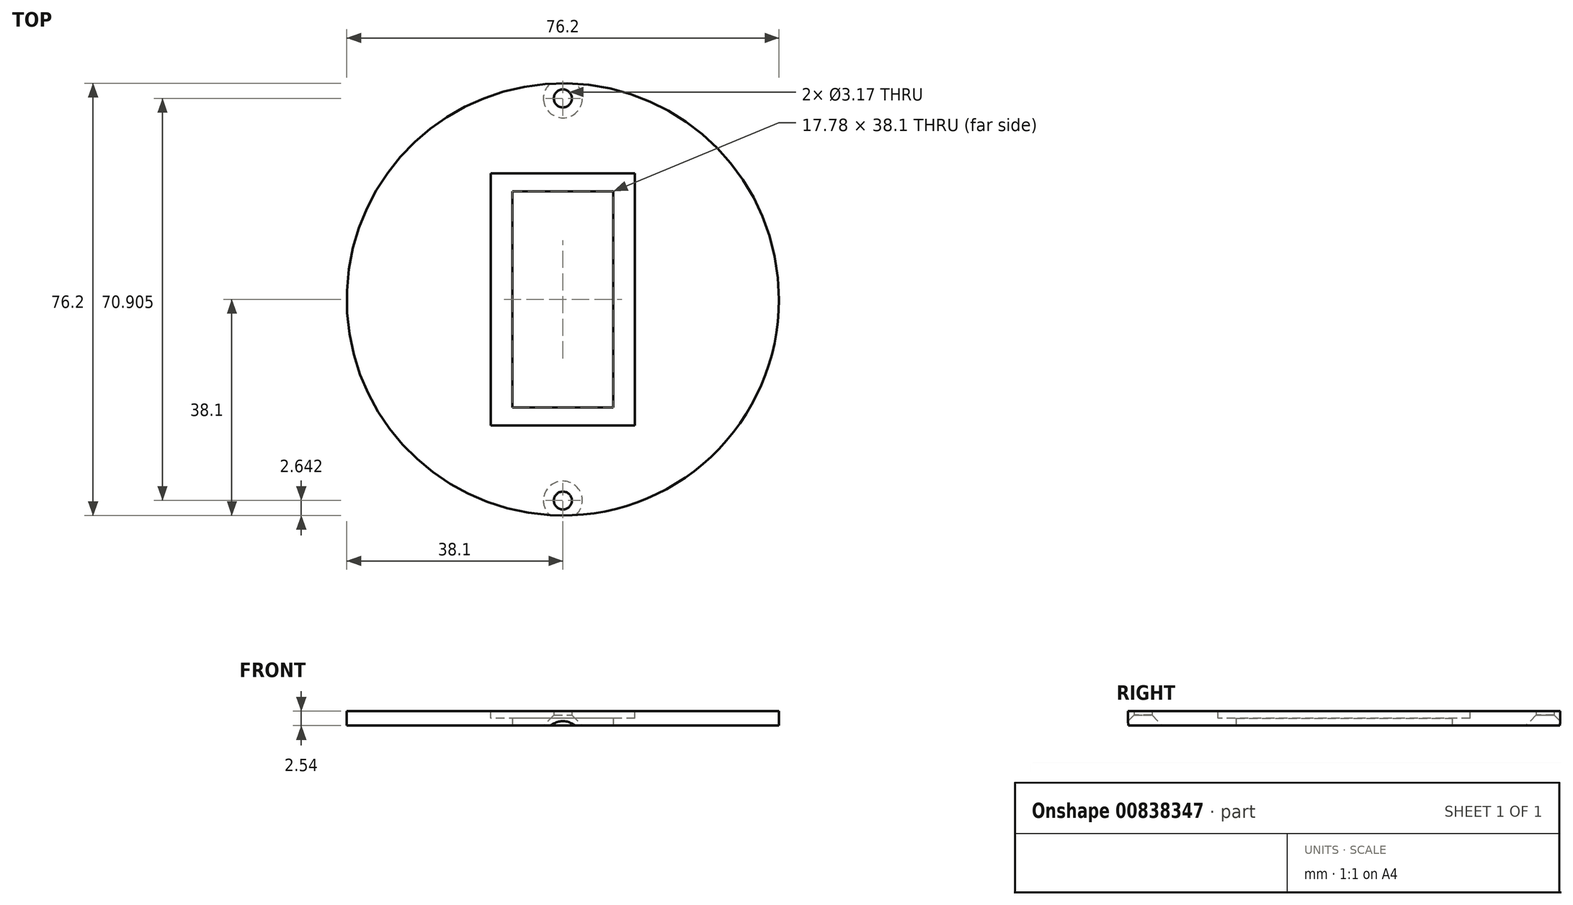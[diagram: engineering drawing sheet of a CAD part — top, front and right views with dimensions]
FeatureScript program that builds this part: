
annotation { "Feature Type Name" : "Feature", "Feature Type Description" : "" }
export const myFeature = defineFeature(function(context is Context, id is Id, definition is map)
    precondition{}
    {
        {
            var Q0;
            Q0=qCreatedBy(makeId("Top.planeOp"),FACE);
            var sketch = newSketch(context, id + "F0", { "sketchPlane" : qUnion([Q0])});
            skCircle(sketch, "E0", {"center": v(0, 0) * mm, "radius": 38.1 * mm});
            skLineSegment(sketch, "E1.bottom", {"start": v(8.9, -19.05) * mm, "end": v(-8.89, -19.05) * mm});
            skLineSegment(sketch, "E1.top", {"start": v(8.9, 19.05) * mm, "end": v(-8.89, 19.05) * mm});
            skLineSegment(sketch, "E1.left", {"start": v(8.9, -19.05) * mm, "end": v(8.9, 19.05) * mm});
            skLineSegment(sketch, "E1.right", {"start": v(-8.89, -19.05) * mm, "end": v(-8.89, 19.05) * mm});
            skSolve(sketch);
        }
        {
            var Q0;
            Q0=qCreatedBy(makeId("Top.planeOp"),FACE);
            var sketch = newSketch(context, id + "F1", { "sketchPlane" : qUnion([Q0])});
            skPoint(sketch, "E2", {"position": v(0, 35.45) * mm});
            skPoint(sketch, "E3", {"position": v(0, -35.46) * mm});
            skSolve(sketch);
        }
        {
            var Q0;
            Q0=makeQuery(id+"F0.imprint","IMPRINT",FACE,{"disambiguationData":[TD([[makeQuery(id+"F0.imprint","IMPRINT",EDGE,{"derivedFrom":sQuery(id+"F0.wireOp",EDGE,"E0")}),1.0]])]});
            extrude(context, id + "F2", {"entities" : qUnion([Q0]), "depth" : 2.54 * mm, "offsetDistance" : 25.4 * mm});
        }
        {
            var Q0;
            Q0=sQuery(id+"F1.wireOp",VERTEX,"E3");
            var Q1;
            Q1=sQuery(id+"F1.wireOp",VERTEX,"E2");
            var Q2;
            Q2=makeQuery(id+"F2.opExtrude","SWEPT_BODY",BODY,{"disambiguationData":[OSD([sQuery(id+"F0.wireOp",EDGE,"E0"),sQuery(id+"F0.wireOp",EDGE,"E1.bottom"),sQuery(id+"F0.wireOp",EDGE,"E1.top"),sQuery(id+"F0.wireOp",EDGE,"E1.left"),sQuery(id+"F0.wireOp",EDGE,"E1.right")])]});
            hole(context, id + "F3", {"style" : HoleStyle.C_SINK, "endStyle" : HoleEndStyle.THROUGH, "oppositeDirection" : true, "holeDiameter" : 3.17 * mm, "cSinkDiameter" : 6.86 * mm, "cSinkAngle" : 90 * degree, "majorDiameter" : 6.35 * mm, "isTappedThrough" : true, "tappedDepth" : 12.7 * mm, "tapClearance" : 3, "locations" : qUnion([Q0, Q1]), "scope" : qUnion([Q2])});
        }
        {
            var Q0;
            Q0=makeQuery(id+"F2.opExtrude","CAP_FACE",FACE,{"disambiguationData":[OSD([sQuery(id+"F0.wireOp",EDGE,"E0"),sQuery(id+"F0.wireOp",EDGE,"E1.bottom"),sQuery(id+"F0.wireOp",EDGE,"E1.top"),sQuery(id+"F0.wireOp",EDGE,"E1.left"),sQuery(id+"F0.wireOp",EDGE,"E1.right")])],"isStart":false});
            var sketch = newSketch(context, id + "F4", { "sketchPlane" : qUnion([Q0])});
            skLineSegment(sketch, "E4.bottom", {"start": v(12.7, 22.23) * mm, "end": v(-12.7, 22.23) * mm});
            skLineSegment(sketch, "E4.top", {"start": v(12.7, -22.23) * mm, "end": v(-12.7, -22.23) * mm});
            skLineSegment(sketch, "E4.left", {"start": v(12.7, 22.23) * mm, "end": v(12.7, -22.23) * mm});
            skLineSegment(sketch, "E4.right", {"start": v(-12.7, 22.23) * mm, "end": v(-12.7, -22.23) * mm});
            skPoint(sketch, "E4.middle", {"position": v(0, 0) * mm});
            skSolve(sketch);
        }
        {
            var Q0;
            Q0=makeQuery(id+"F4.imprint","IMPRINT",FACE,{"disambiguationData":[TD([[makeQuery(id+"F4.imprint","IMPRINT",EDGE,{"derivedFrom":sQuery(id+"F4.wireOp",EDGE,"E4.bottom")}),1.0]])]});
            extrude(context, id + "F5", {"entities" : qUnion([Q0]), "operationType" : NewBodyOperationType.REMOVE, "oppositeDirection" : true, "depth" : 1.27 * mm, "offsetDistance" : 25.4 * mm});
        }
    });
